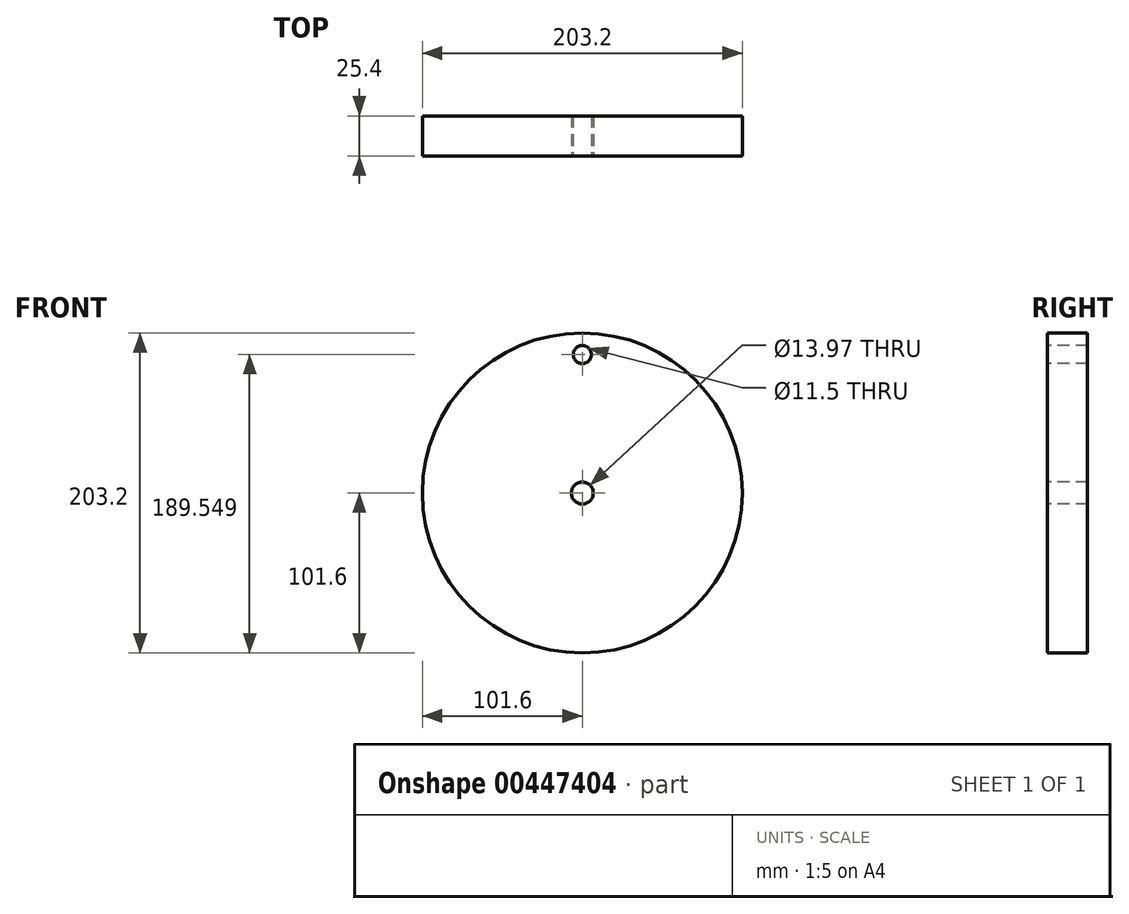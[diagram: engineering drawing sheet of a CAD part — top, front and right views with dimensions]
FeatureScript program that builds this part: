
annotation { "Feature Type Name" : "Feature", "Feature Type Description" : "" }
export const myFeature = defineFeature(function(context is Context, id is Id, definition is map)
    precondition{}
    {
        {
            var Q0;
            Q0=qCreatedBy(makeId("Front.planeOp"),FACE);
            var sketch = newSketch(context, id + "F0", { "sketchPlane" : qUnion([Q0])});
            skCircle(sketch, "E0", {"center": v(0, 0) * mm, "radius": 101.6 * mm});
            skSolve(sketch);
        }
        {
            var Q0;
            Q0 = qSketchRegion(id + "F0", true);
            extrude(context, id + "F1", {"entities" : qUnion([Q0]), "depth" : 25.4 * mm});
        }
        {
            var Q0;
            Q0=makeQuery(id+"F1.opExtrude","CAP_FACE",FACE,{"disambiguationData":[OSD([sQuery(id+"F0.wireOp",EDGE,"E0")])],"isStart":false});
            var sketch = newSketch(context, id + "F2", { "sketchPlane" : qUnion([Q0])});
            skCircle(sketch, "E1", {"center": v(0, 0) * mm, "radius": 6.99 * mm});
            skSolve(sketch);
        }
        {
            var Q0;
            Q0 = qSketchRegion(id + "F2", true);
            extrude(context, id + "F3", {"entities" : qUnion([Q0]), "operationType" : NewBodyOperationType.REMOVE, "oppositeDirection" : true, "depth" : 25.4 * mm});
        }
        {
            var Q0;
            Q0=makeQuery(id+"F1.opExtrude","CAP_FACE",FACE,{"disambiguationData":[OSD([sQuery(id+"F0.wireOp",EDGE,"E0")])],"isStart":false});
            var sketch = newSketch(context, id + "F4", { "sketchPlane" : qUnion([Q0])});
            skLineSegment(sketch, "E2.bottom", {"start": v(-82.18, 59.74) * mm, "end": v(-107.86, 59.74) * mm});
            skLineSegment(sketch, "E2.top", {"start": v(-82.18, 46.35) * mm, "end": v(-107.86, 46.35) * mm});
            skLineSegment(sketch, "E2.left", {"start": v(-82.18, 59.74) * mm, "end": v(-82.18, 46.35) * mm});
            skLineSegment(sketch, "E2.right", {"start": v(-107.86, 59.74) * mm, "end": v(-107.86, 46.35) * mm});
            skSolve(sketch);
        }
        {
            var Q0;
            {var subQ0=sQuery(id+"F4.wireOp",EDGE,"E2.bottom");Q0=makeQuery(id+"F4.imprint","IMPRINT",FACE,{"disambiguationData":[TD([[makeQuery(id+"F4.imprint","IMPRINT",EDGE,{"derivedFrom":subQ0}),1.0]])]});}
            extrude(context, id + "F5", {"entities" : qUnion([Q0]), "operationType" : NewBodyOperationType.REMOVE, "oppositeDirection" : true, "depth" : 25.4 * mm});
        }
        {
            var Q0;
            Q0=makeQuery(id+"F1.opExtrude","CAP_FACE",FACE,{"disambiguationData":[OSD([sQuery(id+"F0.wireOp",EDGE,"E0")])],"isStart":false});
            var sketch = newSketch(context, id + "F6", { "sketchPlane" : qUnion([Q0])});
            skCircle(sketch, "E3", {"center": v(0, 87.95) * mm, "radius": 5.75 * mm});
            skSolve(sketch);
        }
        {
            var Q0;
            Q0=makeQuery(id+"F6.imprint","IMPRINT",FACE,{"disambiguationData":[TD([[makeQuery(id+"F6.imprint","IMPRINT",EDGE,{"derivedFrom":sQuery(id+"F6.wireOp",EDGE,"E3")}),1.0]])]});
            extrude(context, id + "F7", {"entities" : qUnion([Q0]), "operationType" : NewBodyOperationType.REMOVE, "oppositeDirection" : true, "depth" : 25.4 * mm});
        }
    });
